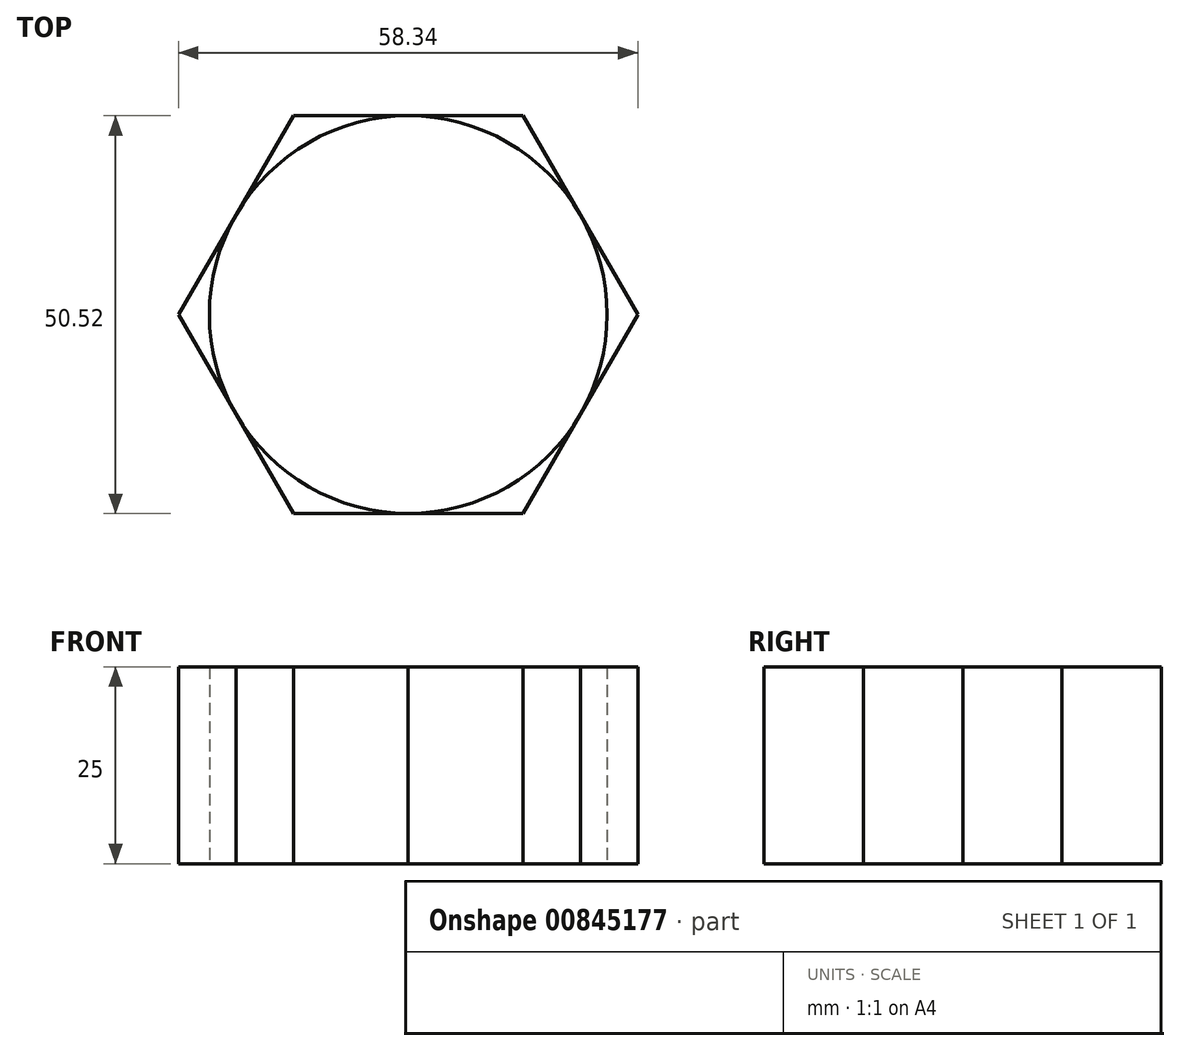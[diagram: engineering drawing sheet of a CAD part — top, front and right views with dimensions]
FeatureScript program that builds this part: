
annotation { "Feature Type Name" : "Feature", "Feature Type Description" : "" }
export const myFeature = defineFeature(function(context is Context, id is Id, definition is map)
    precondition{}
    {
        {
            var Q0;
            Q0=qCreatedBy(makeId("Top.planeOp"),FACE);
            var sketch = newSketch(context, id + "F0", { "sketchPlane" : qUnion([Q0])});
            skCircle(sketch, "E0.cCircle", {"center": v(0, 0) * mm, "radius": 25.26 * mm, "construction": true});
            skLineSegment(sketch, "E0.0", {"start": v(14.59, -25.26) * mm, "end": v(-14.59, -25.26) * mm});
            skLineSegment(sketch, "E0.1", {"start": v(-14.59, -25.26) * mm, "end": v(-29.17, 0) * mm});
            skLineSegment(sketch, "E0.2", {"start": v(-29.17, 0) * mm, "end": v(-14.59, 25.26) * mm});
            skLineSegment(sketch, "E0.3", {"start": v(-14.59, 25.26) * mm, "end": v(14.59, 25.26) * mm});
            skLineSegment(sketch, "E0.4", {"start": v(14.59, 25.26) * mm, "end": v(29.17, 0) * mm});
            skLineSegment(sketch, "E0.5", {"start": v(29.17, 0) * mm, "end": v(14.59, -25.26) * mm});
            skPoint(sketch, "E0.0.midPoint", {"position": v(0, -25.26) * mm});
            skCircle(sketch, "E1", {"center": v(0, 0) * mm, "radius": 25.26 * mm});
            skCircle(sketch, "E2.cCircle", {"center": v(0, 0) * mm, "radius": 21.52 * mm, "construction": true});
            skLineSegment(sketch, "E2.0", {"start": v(12.42, -21.52) * mm, "end": v(-12.42, -21.52) * mm});
            skLineSegment(sketch, "E2.1", {"start": v(-12.42, -21.52) * mm, "end": v(-24.85, 0) * mm});
            skLineSegment(sketch, "E2.2", {"start": v(-24.85, 0) * mm, "end": v(-12.42, 21.52) * mm});
            skLineSegment(sketch, "E2.3", {"start": v(-12.42, 21.52) * mm, "end": v(12.42, 21.52) * mm});
            skLineSegment(sketch, "E2.4", {"start": v(12.42, 21.52) * mm, "end": v(24.85, 0) * mm});
            skLineSegment(sketch, "E2.5", {"start": v(24.85, 0) * mm, "end": v(12.42, -21.52) * mm});
            skPoint(sketch, "E2.0.midPoint", {"position": v(0, -21.52) * mm});
            skCircle(sketch, "E3", {"center": v(0, 0) * mm, "radius": 21.52 * mm});
            skCircle(sketch, "E4.cCircle", {"center": v(0, 0) * mm, "radius": 18.71 * mm, "construction": true});
            skLineSegment(sketch, "E4.0", {"start": v(10.8, -18.71) * mm, "end": v(-10.8, -18.71) * mm});
            skLineSegment(sketch, "E4.1", {"start": v(-10.8, -18.71) * mm, "end": v(-21.6, 0) * mm});
            skLineSegment(sketch, "E4.2", {"start": v(-21.6, 0) * mm, "end": v(-10.8, 18.71) * mm});
            skLineSegment(sketch, "E4.3", {"start": v(-10.8, 18.71) * mm, "end": v(10.8, 18.71) * mm});
            skLineSegment(sketch, "E4.4", {"start": v(10.8, 18.71) * mm, "end": v(21.6, 0) * mm});
            skLineSegment(sketch, "E4.5", {"start": v(21.6, 0) * mm, "end": v(10.8, -18.71) * mm});
            skPoint(sketch, "E4.0.midPoint", {"position": v(0, -18.71) * mm});
            skCircle(sketch, "E5", {"center": v(0, 0) * mm, "radius": 18.71 * mm});
            skCircle(sketch, "E6.cCircle", {"center": v(0, 0) * mm, "radius": 15.6 * mm, "construction": true});
            skLineSegment(sketch, "E6.0", {"start": v(9, -15.6) * mm, "end": v(-9, -15.6) * mm});
            skLineSegment(sketch, "E6.1", {"start": v(-9, -15.6) * mm, "end": v(-18, 0) * mm});
            skLineSegment(sketch, "E6.2", {"start": v(-18, 0) * mm, "end": v(-9, 15.6) * mm});
            skLineSegment(sketch, "E6.3", {"start": v(-9, 15.6) * mm, "end": v(9, 15.6) * mm});
            skLineSegment(sketch, "E6.4", {"start": v(9, 15.6) * mm, "end": v(18, 0) * mm});
            skLineSegment(sketch, "E6.5", {"start": v(18, 0) * mm, "end": v(9, -15.6) * mm});
            skPoint(sketch, "E6.0.midPoint", {"position": v(0, -15.6) * mm});
            skCircle(sketch, "E7", {"center": v(0, 0) * mm, "radius": 15.6 * mm});
            skCircle(sketch, "E8.cCircle", {"center": v(0, 0) * mm, "radius": 12.79 * mm, "construction": true});
            skLineSegment(sketch, "E8.0", {"start": v(7.38, -12.79) * mm, "end": v(-7.38, -12.79) * mm});
            skLineSegment(sketch, "E8.1", {"start": v(-7.38, -12.79) * mm, "end": v(-14.77, 0) * mm});
            skLineSegment(sketch, "E8.2", {"start": v(-14.77, 0) * mm, "end": v(-7.38, 12.79) * mm});
            skLineSegment(sketch, "E8.3", {"start": v(-7.38, 12.79) * mm, "end": v(7.38, 12.79) * mm});
            skLineSegment(sketch, "E8.4", {"start": v(7.38, 12.79) * mm, "end": v(14.77, 0) * mm});
            skLineSegment(sketch, "E8.5", {"start": v(14.77, 0) * mm, "end": v(7.38, -12.79) * mm});
            skPoint(sketch, "E8.0.midPoint", {"position": v(0, -12.79) * mm});
            skCircle(sketch, "E9", {"center": v(0, 0) * mm, "radius": 12.79 * mm});
            skLineSegment(sketch, "E10.0", {"start": v(7.8, -12.54) * mm, "end": v(-6.96, -13.02) * mm});
            skLineSegment(sketch, "E10.1", {"start": v(-6.96, -13.02) * mm, "end": v(-14.76, -0.49) * mm});
            skLineSegment(sketch, "E10.2", {"start": v(-14.76, -0.49) * mm, "end": v(-7.8, 12.54) * mm});
            skLineSegment(sketch, "E10.3", {"start": v(-7.8, 12.54) * mm, "end": v(6.96, 13.02) * mm});
            skLineSegment(sketch, "E10.4", {"start": v(6.96, 13.02) * mm, "end": v(14.76, 0.49) * mm});
            skLineSegment(sketch, "E10.5", {"start": v(14.76, 0.49) * mm, "end": v(7.8, -12.54) * mm});
            skPoint(sketch, "E10.0.midPoint", {"position": v(0.42, -12.78) * mm});
            skSolve(sketch);
        }
        {
            var Q0;
            {var subQ0=sQuery(id+"F0.wireOp",EDGE,"E0.5");var subQ1=sQuery(id+"F0.wireOp",EDGE,"E0.0");var subQ2=makeQuery(id+"F0.imprint","INTERSECT",VERTEX,{"derivedFrom":[subQ1,subQ0]});Q0=makeQuery(id+"F0.imprint","IMPRINT",FACE,{"disambiguationData":[TD([[makeQuery(id+"F0.imprint","IMPRINT",EDGE,{"disambiguationData":[TD([[subQ2,-1.0]])],"derivedFrom":subQ1}),-1.0]])]});}
            var Q1;
            {var subQ0=sQuery(id+"F0.wireOp",EDGE,"E0.1");var subQ1=sQuery(id+"F0.wireOp",EDGE,"E0.0");var subQ2=makeQuery(id+"F0.imprint","INTERSECT",VERTEX,{"derivedFrom":[subQ1,subQ0]});Q1=makeQuery(id+"F0.imprint","IMPRINT",FACE,{"disambiguationData":[TD([[makeQuery(id+"F0.imprint","IMPRINT",EDGE,{"disambiguationData":[TD([[subQ2,1.0]])],"derivedFrom":subQ1}),-1.0]])]});}
            var Q2;
            {var subQ0=sQuery(id+"F0.wireOp",EDGE,"E0.2");var subQ1=sQuery(id+"F0.wireOp",EDGE,"E0.1");var subQ2=makeQuery(id+"F0.imprint","INTERSECT",VERTEX,{"derivedFrom":[subQ1,subQ0]});Q2=makeQuery(id+"F0.imprint","IMPRINT",FACE,{"disambiguationData":[TD([[makeQuery(id+"F0.imprint","IMPRINT",EDGE,{"disambiguationData":[TD([[subQ2,1.0]])],"derivedFrom":subQ1}),-1.0]])]});}
            var Q3;
            {var subQ0=sQuery(id+"F0.wireOp",EDGE,"E0.3");var subQ1=sQuery(id+"F0.wireOp",EDGE,"E0.2");var subQ2=makeQuery(id+"F0.imprint","INTERSECT",VERTEX,{"derivedFrom":[subQ1,subQ0]});Q3=makeQuery(id+"F0.imprint","IMPRINT",FACE,{"disambiguationData":[TD([[makeQuery(id+"F0.imprint","IMPRINT",EDGE,{"disambiguationData":[TD([[subQ2,1.0]])],"derivedFrom":subQ1}),-1.0]])]});}
            var Q4;
            {var subQ0=sQuery(id+"F0.wireOp",EDGE,"E0.5");var subQ1=sQuery(id+"F0.wireOp",EDGE,"E0.4");var subQ2=makeQuery(id+"F0.imprint","INTERSECT",VERTEX,{"derivedFrom":[subQ1,subQ0]});Q4=makeQuery(id+"F0.imprint","IMPRINT",FACE,{"disambiguationData":[TD([[makeQuery(id+"F0.imprint","IMPRINT",EDGE,{"disambiguationData":[TD([[subQ2,1.0]])],"derivedFrom":subQ1}),-1.0]])]});}
            var Q5;
            {var subQ0=sQuery(id+"F0.wireOp",EDGE,"E0.4");var subQ1=sQuery(id+"F0.wireOp",EDGE,"E0.3");var subQ2=makeQuery(id+"F0.imprint","INTERSECT",VERTEX,{"derivedFrom":[subQ1,subQ0]});Q5=makeQuery(id+"F0.imprint","IMPRINT",FACE,{"disambiguationData":[TD([[makeQuery(id+"F0.imprint","IMPRINT",EDGE,{"disambiguationData":[TD([[subQ2,1.0]])],"derivedFrom":subQ1}),-1.0]])]});}
            extrude(context, id + "F1", {"entities" : qUnion([Q0, Q1, Q2, Q3, Q4, Q5]), "depth" : 25 * mm, "offsetDistance" : 25 * mm});
        }
    });
